# Revit family: 633-00-001-DN40-700
name_source: partatom
category: Pipe Accessories
units: mm (PartAtom-declared; Revit-internal decimal feet)

## family parameters
Always vertical = No
Cut with Voids When Loaded = No
Part Type = Valve - Breaks Into
Round Connector Dimension = Use Diameter
Shared = No
Work Plane-Based = No

## types (19) — shared parameters
Body_wallthickness = 10 mm  [stored 0.0328084 ft]
DN040-050_PN16 = 633-071-00-006
DN050-065_PN16 = 633-091-00-006
DN080_PN 16 = 633-106-00-006
DN080_PN16 = 633-133-01-006
DN100_PN 16 = 633-161-00-006
DN100_PN16 = 633-133-00-006
DN150_PN 16 = 633-161-01-006
DN150_PN16 = 633-188-00-006
DN200_PN 16 = 633-257-01-006
DN200_PN16 = 633-227-00-006
DN250_PN 16 = 633-257-00-006
DN250_PN16 = 633-301-00-006
DN300_PN16 = 633-356-00-006
DN350_PN16 = 633-396-00-006
DN400_PN16 = 633-442-00-006
DN450_PN16 = 633-510-00-006
DN500_PN16 = 633-552-00-006
DN600_PN16 = 633-652-00-006
DN700_PN16 = 633-745-00-006
Description_ = AVK SUPA MAXI™ FLANGE ADAPTOR
Search_table = 633-00-001-DN40-700
URL product pages = https://www.avkvalves.com

## per-type parameters (varying)
| type | D | DN | DN_ref | Flange_thickness | H3 | H3_Ref | ID | L | L_ref | Seal_range | Seal_range_ref |
| 633-071-00-006_DN040-050_PN16 | 200 mm | 40.5 mm  [stored 0.132874 ft] | 29 mm  [stored 0.0951444 ft] | 9.5 mm  [stored 0.031168 ft] | 82.5 mm | 45 mm  [stored 0.147638 ft] | 20.25 mm  [stored 0.066437 ft] | 197 mm | 98.5 mm | 30 mm  [stored 0.0984252 ft] | 60 mm  [stored 0.19685 ft] |
| 633-091-00-006_DN050-065_PN16 | 226 mm | 50.65 mm  [stored 0.166175 ft] | 39 mm  [stored 0.127953 ft] | 9.5 mm  [stored 0.031168 ft] | 92.5 mm  [stored 0.303478 ft] | 55 mm  [stored 0.180446 ft] | 25.33 mm | 197 mm | 98.5 mm | 40 mm  [stored 0.131234 ft] | 80 mm  [stored 0.262467 ft] |
| 633-106-00-006_DN080_PN 16 | 235 mm | 80 mm  [stored 0.262467 ft] | 46 mm  [stored 0.150919 ft] | 9.5 mm  [stored 0.031168 ft] | 100 mm | 62 mm  [stored 0.203412 ft] | 40 mm  [stored 0.131234 ft] | 198 mm | 99 mm | 47 mm  [stored 0.154199 ft] | 94 mm |
| 633-133-00-006_DN100_PN 16 | 268 mm | 100 mm | 58.5 mm  [stored 0.191929 ft] | 9.5 mm  [stored 0.031168 ft] | 114.5 mm | 74.5 mm  [stored 0.244423 ft] | 50 mm  [stored 0.164042 ft] | 203 mm | 101.5 mm | 59.5 mm  [stored 0.19521 ft] | 119 mm |
| 633-161-01-006_DN150_PN 16 | 285 mm | 150 mm | 72 mm  [stored 0.23622 ft] | 9.5 mm  [stored 0.031168 ft] | 142.5 mm | 88 mm  [stored 0.288714 ft] | 75 mm | 198 mm | 99 mm | 73 mm  [stored 0.239501 ft] | 146 mm |
| 633-188-00-006_DN150_PN16 | 340 mm | 150.1 mm | 86 mm  [stored 0.282152 ft] | 10 mm  [stored 0.0328084 ft] | 142.5 mm | 102 mm | 75.05 mm | 220 mm | 110 mm | 87 mm  [stored 0.285433 ft] | 174 mm |
| 633-257-01-006_DN200_PN16 | 437 mm | 200.1 mm | 122 mm | 13.25 mm  [stored 0.0434711 ft] | 171.5 mm | 138 mm | 100.05 mm | 245 mm | 122.5 mm | 123 mm | 246 mm |
| 633-257-00-006_DN250_PN 16 | 437 mm | 250 mm | 122 mm | 12.25 mm  [stored 0.0401903 ft] | 203 mm | 138 mm | 125 mm | 245 mm | 122.5 mm | 123 mm | 246 mm |
| 633-227-00-006_DN200_PN 16 | 389 mm | 200 mm | 104 mm | 11 mm  [stored 0.0360892 ft] | 171.5 mm | 120 mm | 100 mm | 243 mm | 121.5 mm | 105 mm | 210 mm |
| 633-301-00-006_DN250_PN16 | 476 mm | 250.1 mm | 141 mm | 14 mm  [stored 0.0459318 ft] | 203 mm | 157 mm | 125.05 mm | 254 mm | 127 mm | 142 mm | 284 mm |
| 633-356-00-006_DN300_PN16 | 545 mm | 300 mm | 166.5 mm | 15 mm  [stored 0.0492126 ft] | 241.5 mm | 182.5 mm | 150 mm | 282 mm | 141 mm | 167.5 mm | 335 mm |
| 633-396-00-006_DN350_PN16 | 612 mm | 350 mm | 187 mm | 15.75 mm  [stored 0.0516732 ft] | 270 mm | 203 mm | 175 mm | 419 mm | 209.5 mm | 188 mm | 376 mm |
| 633-442-00-006_DN400_PN16 | 661 mm | 400 mm | 207.5 mm | 15.75 mm  [stored 0.0516732 ft] | 298.5 mm | 223.5 mm | 200 mm | 447 mm | 223.5 mm | 208.5 mm | 417 mm |
| 633-510-00-006_DN450_PN16 | 740 mm | 450 mm | 247.5 mm | 18 mm  [stored 0.0590551 ft] | 330 mm | 263.5 mm | 225 mm | 614 mm | 307 mm | 248.5 mm | 497 mm |
| 633-552-00-006_DN500_PN16 | 772 mm | 500 mm | 261.5 mm | 18 mm  [stored 0.0590551 ft] | 367.5 mm | 277.5 mm | 250 mm | 605 mm | 302.5 mm | 262.5 mm | 525 mm |
| 633-652-00-006_DN600_PN16 | 872 mm | 600 mm | 313 mm | 18 mm  [stored 0.0590551 ft] | 425 mm | 329 mm | 300 mm | 634 mm | 317 mm | 314 mm | 628 mm |
| 633-745-00-006_DN700_PN16 | 991 mm | 700 mm | 360.5 mm | 18 mm  [stored 0.0590551 ft] | 460 mm | 376.5 mm | 350 mm | 650 mm | 325 mm | 361.5 mm | 723 mm |
| 633-133-01-006_DN080_PN16 | 268 mm | 80.1 mm  [stored 0.262795 ft] | 58.5 mm  [stored 0.191929 ft] | 9.5 mm  [stored 0.031168 ft] | 100 mm | 74.5 mm  [stored 0.244423 ft] | 40.05 mm  [stored 0.131398 ft] | 210 mm | 105 mm | 59.5 mm  [stored 0.19521 ft] | 119 mm |
| 633-161-00-006_DN100_PN16 | 285 mm | 100.1 mm | 72 mm  [stored 0.23622 ft] | 9.5 mm  [stored 0.031168 ft] | 114.5 mm | 88 mm  [stored 0.288714 ft] | 50.05 mm  [stored 0.164206 ft] | 198 mm | 99 mm | 73 mm  [stored 0.239501 ft] | 146 mm |

note: [stored X ft] marks values corroborated as IEEE doubles in the binary element streams (Revit-internal decimal feet)

## geometry (parser evidence)
native form markers: Extrusion x1, Sweep x9
no freeform markers — native parametric forms only
